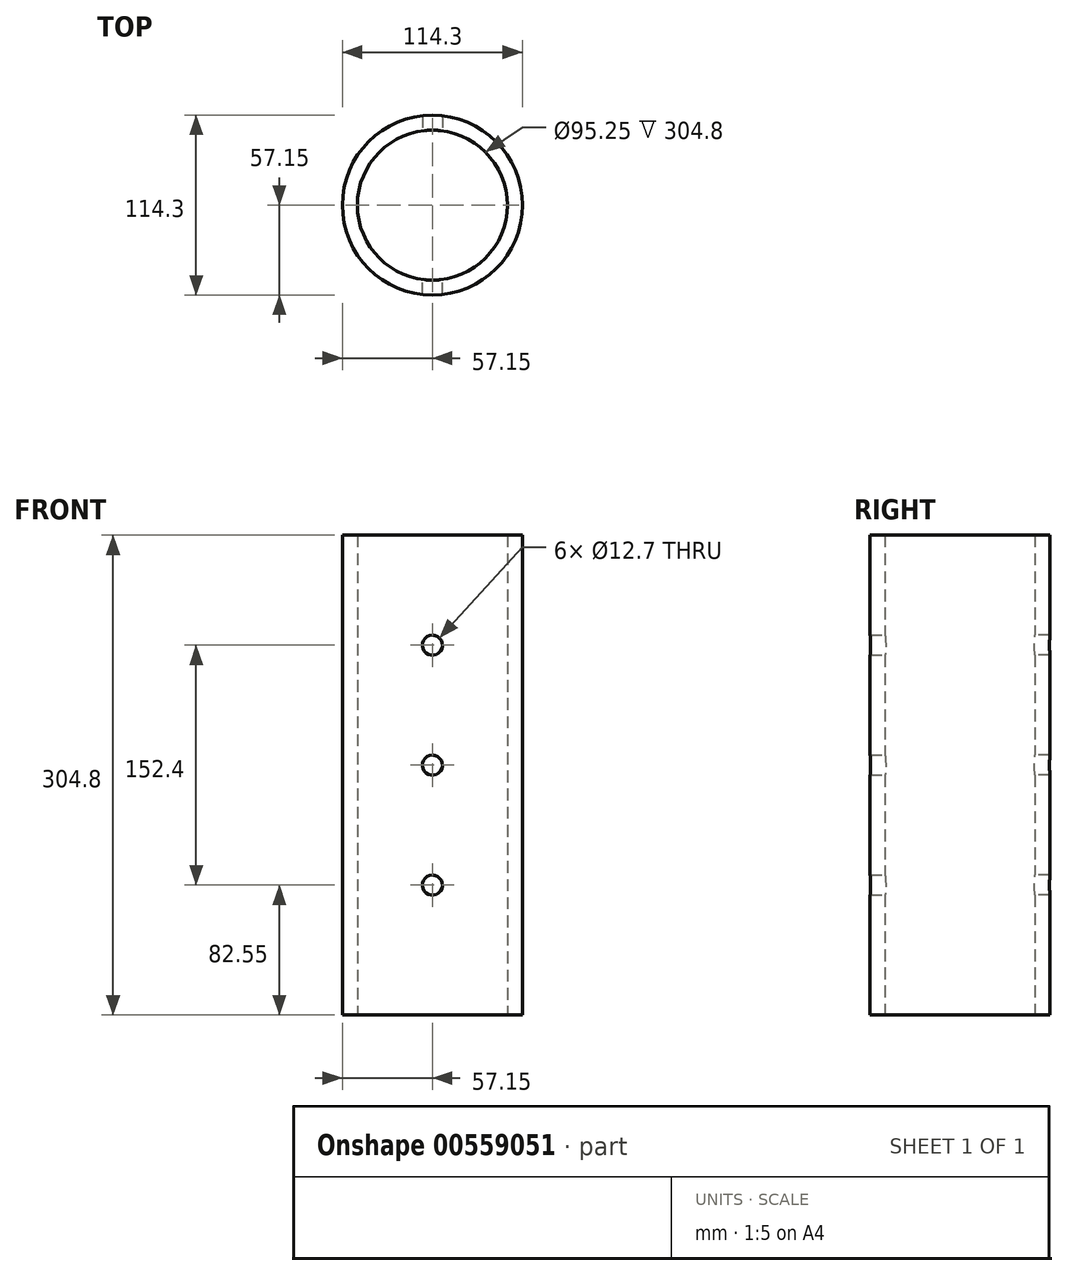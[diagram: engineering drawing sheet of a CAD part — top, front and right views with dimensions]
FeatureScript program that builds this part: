
annotation { "Feature Type Name" : "Feature", "Feature Type Description" : "" }
export const myFeature = defineFeature(function(context is Context, id is Id, definition is map)
    precondition{}
    {
        {
            var Q0;
            Q0=qCreatedBy(makeId("Top.planeOp"),FACE);
            var sketch = newSketch(context, id + "F0", { "sketchPlane" : qUnion([Q0])});
            skCircle(sketch, "E0", {"center": v(0, 0) * mm, "radius": 57.15 * mm});
            skCircle(sketch, "E1", {"center": v(0, 0) * mm, "radius": 47.63 * mm});
            skSolve(sketch);
        }
        {
            var Q0;
            Q0 = qSketchRegion(id + "F0", true);
            extrude(context, id + "F1", {"entities" : qUnion([Q0]), "depth" : 304.8 * mm, "offsetDistance" : 25.4 * mm});
        }
        {
            var Q0;
            Q0=qCreatedBy(makeId("Front.planeOp"),FACE);
            var sketch = newSketch(context, id + "F2", { "sketchPlane" : qUnion([Q0])});
            skCircle(sketch, "E2", {"center": v(0, 82.55) * mm, "radius": 6.35 * mm});
            skCircle(sketch, "E3.0.1.0", {"center": v(0, 158.75) * mm, "radius": 6.35 * mm});
            skCircle(sketch, "E3.0.2.0", {"center": v(0, 234.95) * mm, "radius": 6.35 * mm});
            skLineSegment(sketch, "E3.direction1", {"start": v(0, 82.55) * mm, "end": v(25.4, 82.55) * mm, "construction": true});
            skLineSegment(sketch, "E3.direction2", {"start": v(0, 82.55) * mm, "end": v(0, 158.75) * mm, "construction": true});
            skSolve(sketch);
        }
        {
            var Q0;
            Q0 = qSketchRegion(id + "F2", true);
            extrude(context, id + "F3", {"entities" : qUnion([Q0]), "operationType" : NewBodyOperationType.REMOVE, "endBound" : BoundingType.THROUGH_ALL, "oppositeDirection" : true, "depth" : 25.4 * mm, "offsetDistance" : 25.4 * mm});
        }
        {
            var Q0;
            Q0 = qSketchRegion(id + "F2", true);
            extrude(context, id + "F4", {"entities" : qUnion([Q0]), "operationType" : NewBodyOperationType.REMOVE, "endBound" : BoundingType.THROUGH_ALL, "depth" : 25.4 * mm, "offsetDistance" : 25.4 * mm});
        }
    });
